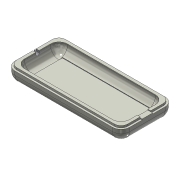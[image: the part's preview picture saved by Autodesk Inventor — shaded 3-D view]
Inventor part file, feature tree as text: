
AUTODESK INVENTOR PART (.ipt)
format: ipt  version: 2022.1 (Build 261234020, 234B)  size: 238,592 bytes
history: native  units: mm
features: extrude x6, sketch x4, fillet x1, other x1
ambient origin geometry x8: Origin, YZ Plane, XZ Plane, XY Plane, X Axis, Y Axis, Z Axis, Center Point
bodies: Solid1 (feature_tree)
feature tree (12):
  sketch  "Sketch1"  dims[d0=120.0mm d1=55.0mm]
  extrude  "Extrusion1"  Depth=55.0mm
  extrude  "Extrusion2"  Depth=5.0mm
  fillet  "Fillet1"  Radius=15.0mm
  extrude  "Extrusion3"  Depth=10.0mm
  other  "Lip1"
  sketch  "Sketch5"  dims[d6=10.0mm d7=0.0mm d8=9.0mm]
  extrude  "Extrusion4"  Depth=3.5mm
  extrude  "Extrusion5"  Depth=3.5mm
  extrude  "Extrusion7"  Depth=3.5mm
  sketch  "Sketch3"  dims[d2=5.0mm d3=5.0mm d4=15.0mm d5=0.0mm]
  sketch  "Sketch7"  dims[d9=17.0mm d10=17.0mm d11=3.5mm d12=45.0mm d13=34.0mm d14=10.0mm d15=0.0mm d16=2.0mm d17=2.0mm d18=0.0mm d19=0.0mm d20=0.872665mm d21=0.0mm d25=4.0mm d26=5.5mm d27=11.0mm d28=3.0mm d29=0.0mm d30=7.0mm d31=0.0mm d35=3.5mm d36=7.0mm d37=0.0mm d32=0.5mm d33=0.872665mm]
